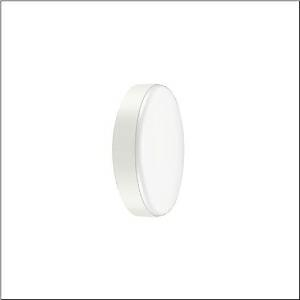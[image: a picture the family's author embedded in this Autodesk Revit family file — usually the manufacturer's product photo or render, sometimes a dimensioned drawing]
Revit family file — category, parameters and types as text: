
# Revit family: round_31_51wc10ma42a
name_source: partatom
category: Lighting Fixtures
units: mm (PartAtom-declared; Revit-internal decimal feet)

## family parameters
Cut with Voids When Loaded = No
Host = Face
Light Source = No
Part Type = Normal
Room Calculation Point = No
Round Connector Dimension = Use Diameter
Shared = No

## types (1)
- --- (1 x LED, 2550 lm, 19 W, 4000K)
    Apparent Load = 19 VA
    CIE Flux Codes = 44 75 94 94 100
    Color Rendering = 80
    Color Temperature = 4000K
    Default Elevation = 1800 mm
    Description = Round 31, wall and ceiling luminaire, primary optical cover: cover, of PC, opal, light emission: direct distribution, primary light characteristic: symmetric, installation type: surface-mounted, LED, rated luminous flux: 2.550lm, luminous efficacy: 134lm/W, light colour: 840, colour temperature: 4000K, control gear: ON/OFF Multilumen, with terminal, 3-pole, max. 2.5mm², mains connection: 220..240V, AC, 50/60Hz, rated input power: 19W, luminaire housing, of PC, traffic white (RAL 9016), diameter: 350mm, protection rating (complete): IP65, insulation class (complete): insulation class II (safety insulation), certification: CE, impact resistance: IK10, permissible operating ambient temperature: -20..+40°C, permissible storage temperature: -20..+60°C, packaging unit: 1 piece
    Height = 97 mm
    Lamp = 1 x LED
    Lamp Light Flux = 2550 lm
    Lamp Power = 19 W
    Lamp count = 1
    Length = 350 mm
    Luminous efficacy = 134 lm/W
    Manufacturer = Siteco
    ModVariant = No
    Model = 51WC10MA42A
    Mounting Place = Ceiling
    Mounting Type = Surface mounted
    Number of Poles = 1
    OnlyDefault = Yes
    Power Factor = 1
    Product Name = Round 31
    Product group = wall and ceiling luminaire | ceiling mounted
    ProductGroupID = 305
    Protection Class = Protection class II
    Protection Degree = IP 65
    RLX_Detail_Level = 1
    RLX_Emergency_Light_Flux = 0 lm
    RLX_Emergency_Type = 0
    RLX_Emergency_Type_DB = No
    RlxData = <blob elided: 31697 chars, md5=f359046c>
    Socket = socket
    Standby Power = 0 W
    System Light Flux = 2550 lm
    System Power = 19 W
    Type Comments = factory setting: luminous flux: 100 % | (ON | ON)
    Type Image = l_1007027.jpg
    URL = http://relux.com
    VarID = @adj_172313
    Voltage = 0 V
    Weight = 0.00 kg
    Width = 0 mm  [stored 0 ft]

note: [stored X ft] marks values corroborated as IEEE doubles in the binary element streams (Revit-internal decimal feet)

## geometry (parser evidence)
native form markers: Blend x4, Sweep x10
no freeform markers — native parametric forms only
